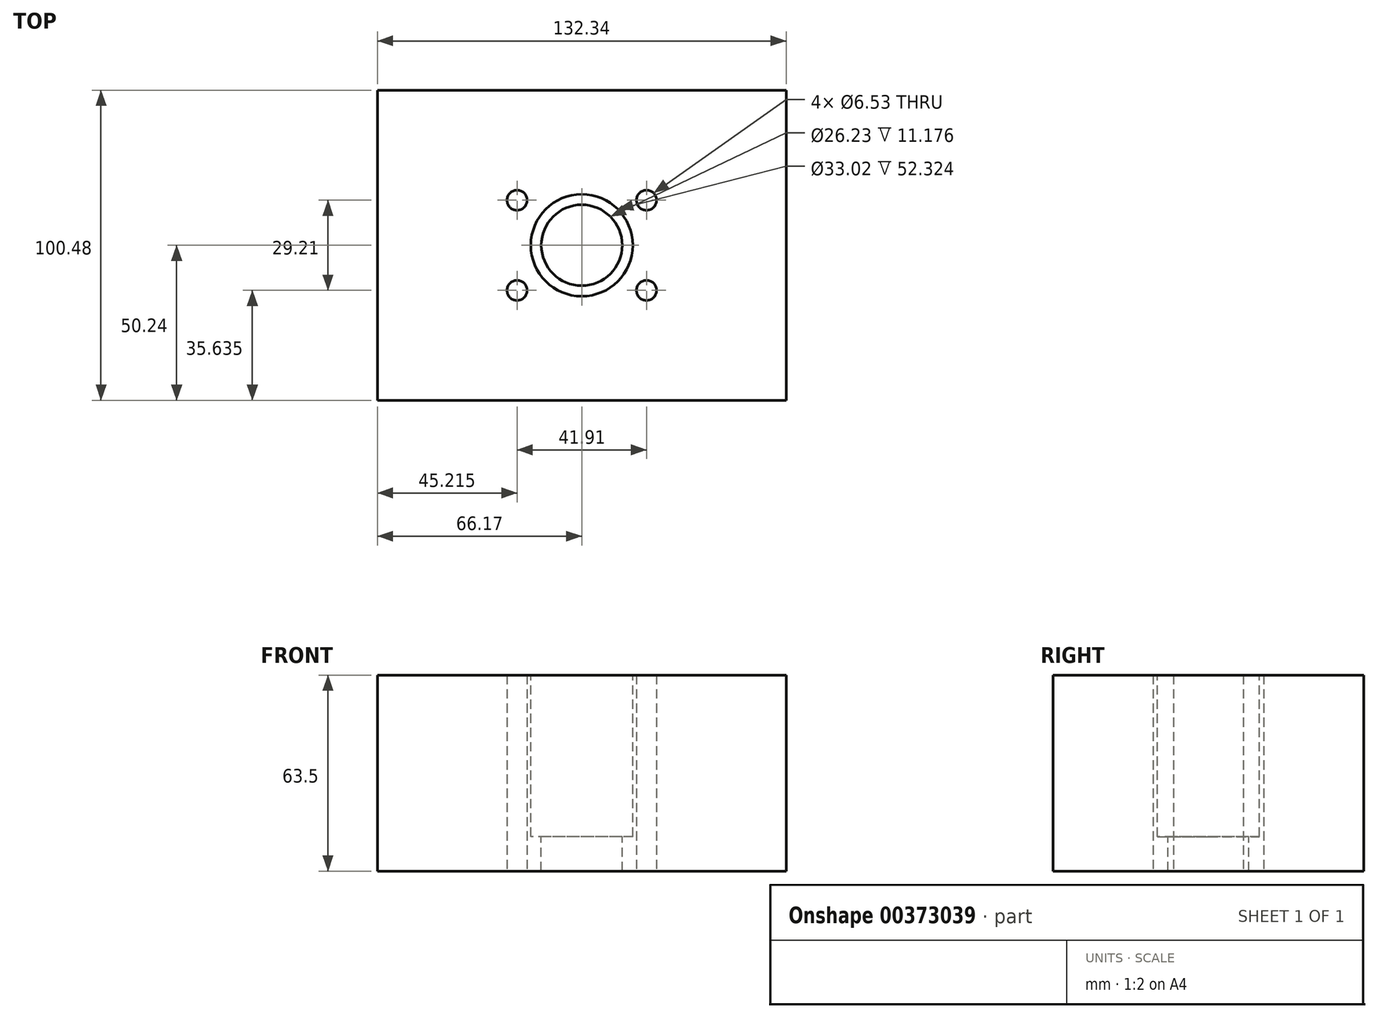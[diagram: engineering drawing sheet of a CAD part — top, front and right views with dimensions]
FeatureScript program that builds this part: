
annotation { "Feature Type Name" : "Feature", "Feature Type Description" : "" }
export const myFeature = defineFeature(function(context is Context, id is Id, definition is map)
    precondition{}
    {
        {
            var Q0;
            Q0=qCreatedBy(makeId("Top.planeOp"),FACE);
            var sketch = newSketch(context, id + "F0", { "sketchPlane" : qUnion([Q0])});
            skLineSegment(sketch, "E0.bottom", {"start": v(-66.17, 50.24) * mm, "end": v(66.17, 50.24) * mm});
            skLineSegment(sketch, "E0.top", {"start": v(-66.17, -50.24) * mm, "end": v(66.17, -50.24) * mm});
            skLineSegment(sketch, "E0.left", {"start": v(-66.17, 50.24) * mm, "end": v(-66.17, -50.24) * mm});
            skLineSegment(sketch, "E0.right", {"start": v(66.17, 50.24) * mm, "end": v(66.17, -50.24) * mm});
            skPoint(sketch, "E0.middle", {"position": v(0, 0) * mm});
            skSolve(sketch);
        }
        {
            var Q0;
            Q0=makeQuery(id+"F0.imprint","IMPRINT",FACE,{"disambiguationData":[TD([[makeQuery(id+"F0.imprint","IMPRINT",EDGE,{"derivedFrom":sQuery(id+"F0.wireOp",EDGE,"E0.bottom")}),-1.0]])]});
            extrude(context, id + "F1", {"entities" : qUnion([Q0]), "depth" : 63.5 * mm});
        }
        {
            var Q0;
            Q0=makeQuery(id+"F1.opExtrude","CAP_FACE",FACE,{"disambiguationData":[OSD([sQuery(id+"F0.wireOp",EDGE,"E0.bottom"),sQuery(id+"F0.wireOp",EDGE,"E0.top"),sQuery(id+"F0.wireOp",EDGE,"E0.left"),sQuery(id+"F0.wireOp",EDGE,"E0.right")])],"isStart":false});
            var sketch = newSketch(context, id + "F2", { "sketchPlane" : qUnion([Q0])});
            skPoint(sketch, "E1", {"position": v(0, 0) * mm});
            skSolve(sketch);
        }
        {
            var Q0;
            Q0=sQuery(id+"F2.wireOp",VERTEX,"E1");
            var Q1;
            Q1=makeQuery(id+"F1.opExtrude","SWEPT_BODY",BODY,{"disambiguationData":[OSD([sQuery(id+"F0.wireOp",EDGE,"E0.bottom"),sQuery(id+"F0.wireOp",EDGE,"E0.top"),sQuery(id+"F0.wireOp",EDGE,"E0.left"),sQuery(id+"F0.wireOp",EDGE,"E0.right")])]});
            hole(context, id + "F3", {"style" : HoleStyle.C_BORE, "endStyle" : HoleEndStyle.THROUGH, "holeDiameter" : 26.23 * mm, "cBoreDiameter" : 33.02 * mm, "cBoreDepth" : 52.32 * mm, "isTappedThrough" : true, "tappedDepth" : 12.7 * mm, "tapClearance" : 3, "startFromSketch" : true, "locations" : qUnion([Q0]), "scope" : qUnion([Q1])});
        }
        {
            var Q0;
            Q0=makeQuery(id+"F1.opExtrude","CAP_FACE",FACE,{"disambiguationData":[OSD([sQuery(id+"F0.wireOp",EDGE,"E0.bottom"),sQuery(id+"F0.wireOp",EDGE,"E0.top"),sQuery(id+"F0.wireOp",EDGE,"E0.left"),sQuery(id+"F0.wireOp",EDGE,"E0.right")])],"isStart":true});
            var sketch = newSketch(context, id + "F4", { "sketchPlane" : qUnion([Q0])});
            skLineSegment(sketch, "E2.bottom", {"start": v(-28.58, 22.22) * mm, "end": v(28.57, 22.23) * mm});
            skLineSegment(sketch, "E2.top", {"start": v(-28.57, -22.23) * mm, "end": v(28.58, -22.23) * mm});
            skLineSegment(sketch, "E2.left", {"start": v(-28.58, 22.22) * mm, "end": v(-28.57, -22.23) * mm});
            skLineSegment(sketch, "E2.right", {"start": v(28.57, 22.23) * mm, "end": v(28.58, -22.22) * mm});
            skPoint(sketch, "E2.middle", {"position": v(0, 0) * mm});
            skPoint(sketch, "E3", {"position": v(-20.96, 14.6) * mm});
            skPoint(sketch, "E4.MirrorP", {"position": v(-20.96, -14.6) * mm});
            skPoint(sketch, "E5.MirrorP", {"position": v(20.96, 14.6) * mm});
            skPoint(sketch, "E6.MirrorP", {"position": v(20.96, -14.6) * mm});
            skSolve(sketch);
        }
        {
            var Q0;
            Q0=sQuery(id+"F4.wireOp",VERTEX,"E3");
            var Q1;
            Q1=sQuery(id+"F4.wireOp",VERTEX,"E4.MirrorP");
            var Q2;
            Q2=sQuery(id+"F4.wireOp",VERTEX,"E6.MirrorP");
            var Q3;
            Q3=sQuery(id+"F4.wireOp",VERTEX,"E5.MirrorP");
            var Q4;
            Q4=makeQuery(id+"F1.opExtrude","SWEPT_BODY",BODY,{"disambiguationData":[OSD([sQuery(id+"F0.wireOp",EDGE,"E0.bottom"),sQuery(id+"F0.wireOp",EDGE,"E0.top"),sQuery(id+"F0.wireOp",EDGE,"E0.left"),sQuery(id+"F0.wireOp",EDGE,"E0.right")])]});
            hole(context, id + "F5", {"style" : HoleStyle.SIMPLE, "endStyle" : HoleEndStyle.THROUGH, "holeDiameter" : 6.53 * mm, "isTappedThrough" : true, "tappedDepth" : 12.7 * mm, "tapClearance" : 3, "startFromSketch" : true, "locations" : qUnion([Q0, Q1, Q2, Q3]), "scope" : qUnion([Q4])});
        }
    });
